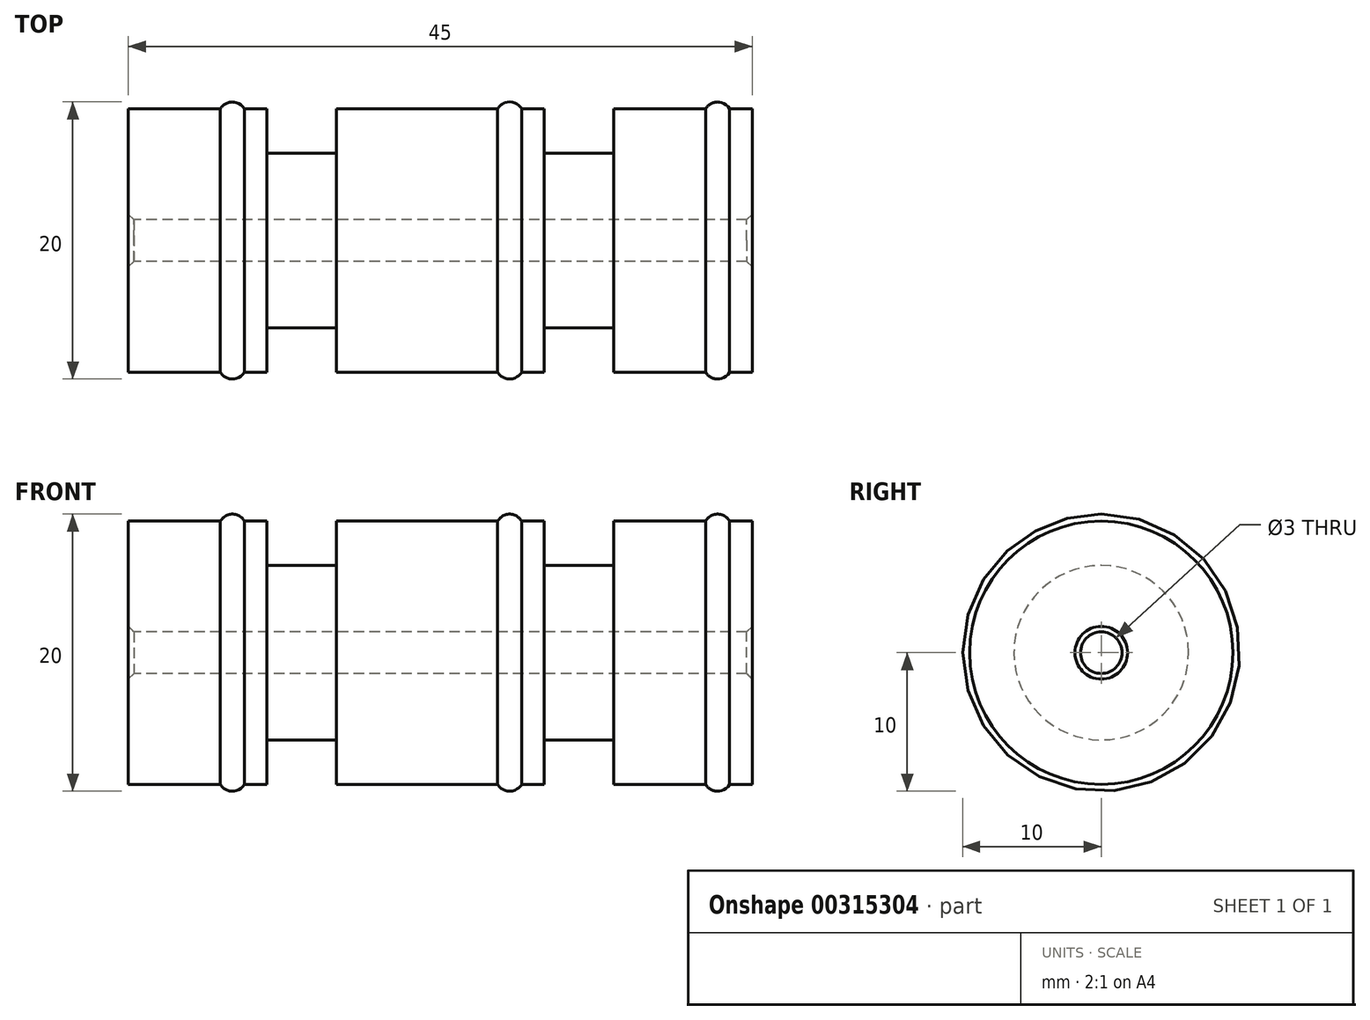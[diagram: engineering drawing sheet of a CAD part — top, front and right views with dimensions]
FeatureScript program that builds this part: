
annotation { "Feature Type Name" : "Feature", "Feature Type Description" : "" }
export const myFeature = defineFeature(function(context is Context, id is Id, definition is map)
    precondition{}
    {
        {
            var Q0;
            Q0=qCreatedBy(makeId("Front.planeOp"),FACE);
            var sketch = newSketch(context, id + "F0", { "sketchPlane" : qUnion([Q0])});
            skLineSegment(sketch, "E0", {"start": v(0, 0) * mm, "end": v(45, 0) * mm, "construction": true});
            skLineSegment(sketch, "E1", {"start": v(0, 6.3) * mm, "end": v(45, 6.3) * mm, "construction": true});
            skLineSegment(sketch, "E2", {"start": v(0, 9.5) * mm, "end": v(45, 9.5) * mm, "construction": true});
            skLineSegment(sketch, "E3", {"start": v(0, 1.5) * mm, "end": v(45, 1.5) * mm, "construction": true});
            skSolve(sketch);
        }
        {
            var Q0;
            Q0=qCreatedBy(makeId("Front.planeOp"),FACE);
            var sketch = newSketch(context, id + "F1", { "sketchPlane" : qUnion([Q0])});
            skLineSegment(sketch, "E4", {"start": v(0, 1.5) * mm, "end": v(45, 1.5) * mm});
            skLineSegment(sketch, "E5", {"start": v(0, 1.5) * mm, "end": v(0, 9.5) * mm});
            skLineSegment(sketch, "E6", {"start": v(45, 9.5) * mm, "end": v(45, 1.5) * mm});
            skLineSegment(sketch, "E7", {"start": v(0, 9.5) * mm, "end": v(10, 9.5) * mm});
            skLineSegment(sketch, "E8", {"start": v(10, 9.5) * mm, "end": v(10, 6.3) * mm});
            skLineSegment(sketch, "E9", {"start": v(10, 6.3) * mm, "end": v(15, 6.3) * mm});
            skLineSegment(sketch, "E10", {"start": v(15, 6.3) * mm, "end": v(15, 9.5) * mm});
            skLineSegment(sketch, "E11", {"start": v(15, 9.5) * mm, "end": v(30, 9.5) * mm});
            skLineSegment(sketch, "E12", {"start": v(30, 9.5) * mm, "end": v(30, 6.3) * mm});
            skLineSegment(sketch, "E13", {"start": v(30, 6.3) * mm, "end": v(35, 6.3) * mm});
            skLineSegment(sketch, "E14", {"start": v(35, 6.3) * mm, "end": v(35, 9.5) * mm});
            skLineSegment(sketch, "E15", {"start": v(35, 9.5) * mm, "end": v(45, 9.5) * mm});
            skCircle(sketch, "E16", {"center": v(7.5, 9) * mm, "radius": 1 * mm});
            skPoint(sketch, "E17", {"position": v(7.5, 10) * mm});
            skCircle(sketch, "E18", {"center": v(27.5, 9) * mm, "radius": 1 * mm});
            skCircle(sketch, "E19", {"center": v(42.5, 9) * mm, "radius": 1 * mm});
            skSolve(sketch);
        }
        {
            var Q0;
            Q0 = qSketchRegion(id + "F1", true);
            var Q1;
            Q1=sQuery(id+"F0.wireOp",EDGE,"E0");
            revolve(context, id + "F2", {"entities" : qUnion([Q0]), "axis" : qUnion([Q1]), "revolveType" : RevolveType.FULL});
        }
        {
            var Q0;
            Q0=makeQuery(id+"F2.opRevolve","SWEPT_EDGE",EDGE,{"disambiguationData":[OSD([sQuery(id+"F1.wireOp",EDGE,"E4"),sQuery(id+"F1.wireOp",EDGE,"E5")])]});
            var Q1;
            Q1=makeQuery(id+"F2.opRevolve","SWEPT_EDGE",EDGE,{"disambiguationData":[OSD([sQuery(id+"F1.wireOp",EDGE,"E4"),sQuery(id+"F1.wireOp",EDGE,"E6")])]});
            chamfer(context, id + "F3", {"entities" : qUnion([Q0, Q1]), "width" : 0.4 * mm, "tangentPropagation" : true});
        }
    });
